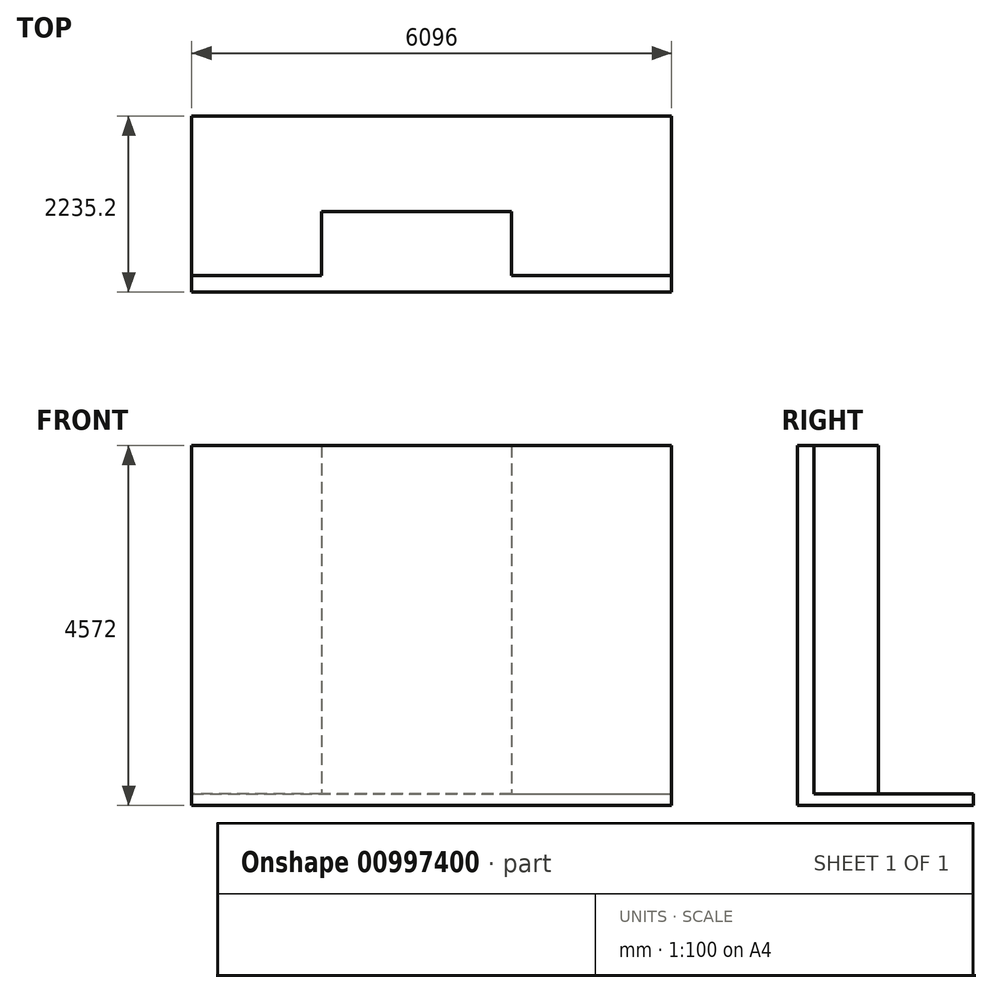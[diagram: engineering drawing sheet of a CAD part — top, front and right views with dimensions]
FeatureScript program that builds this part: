
annotation { "Feature Type Name" : "Feature", "Feature Type Description" : "" }
export const myFeature = defineFeature(function(context is Context, id is Id, definition is map)
    precondition{}
    {
        {
            var Q0;
            Q0=qCreatedBy(makeId("Top.planeOp"),FACE);
            var sketch = newSketch(context, id + "F0", { "sketchPlane" : qUnion([Q0])});
            skLineSegment(sketch, "E0.bottom", {"start": v(-2937.04, -1341.12) * mm, "end": v(3158.96, -1341.12) * mm});
            skLineSegment(sketch, "E0.top", {"start": v(-1290.81, -316.57) * mm, "end": v(1126.96, -316.57) * mm});
            skLineSegment(sketch, "E0.left", {"start": v(-2937.04, -1341.12) * mm, "end": v(-2937.04, -1132.54) * mm});
            skLineSegment(sketch, "E0.right", {"start": v(3158.96, -1341.12) * mm, "end": v(3158.96, -1132.54) * mm});
            skLineSegment(sketch, "E1.top", {"start": v(3158.96, -1132.54) * mm, "end": v(1126.96, -1132.54) * mm});
            skLineSegment(sketch, "E1.right", {"start": v(1126.96, -316.57) * mm, "end": v(1126.96, -1132.54) * mm});
            skLineSegment(sketch, "E2.top", {"start": v(-2937.04, -1132.54) * mm, "end": v(-1290.81, -1132.54) * mm});
            skLineSegment(sketch, "E2.right", {"start": v(-1290.81, -316.57) * mm, "end": v(-1290.81, -1132.54) * mm});
            skSolve(sketch);
        }
        {
            var Q0;
            Q0 = qSketchRegion(id + "F0", true);
            extrude(context, id + "F1", {"entities" : qUnion([Q0]), "depth" : 4572 * mm, "offsetDistance" : 25.4 * mm});
        }
        {
            var Q0;
            Q0=makeQuery(id+"F1.opExtrude","SWEPT_FACE",FACE,{"disambiguationData":[OSD([sQuery(id+"F0.wireOp",EDGE,"E0.bottom")])]});
            var sketch = newSketch(context, id + "F2", { "sketchPlane" : qUnion([Q0])});
            skLineSegment(sketch, "E3.bottom", {"start": v(-2937.04, 0) * mm, "end": v(3158.96, 0) * mm});
            skLineSegment(sketch, "E3.top", {"start": v(-2937.04, 146.8) * mm, "end": v(3158.96, 146.8) * mm});
            skLineSegment(sketch, "E3.left", {"start": v(-2937.04, 0) * mm, "end": v(-2937.04, 146.8) * mm});
            skLineSegment(sketch, "E3.right", {"start": v(3158.96, 0) * mm, "end": v(3158.96, 146.8) * mm});
            skSolve(sketch);
        }
        {
            var Q0;
            Q0 = qSketchRegion(id + "F2", true);
            extrude(context, id + "F3", {"entities" : qUnion([Q0]), "operationType" : NewBodyOperationType.ADD, "oppositeDirection" : true, "depth" : 2235.2 * mm, "offsetDistance" : 25.4 * mm});
        }
    });
